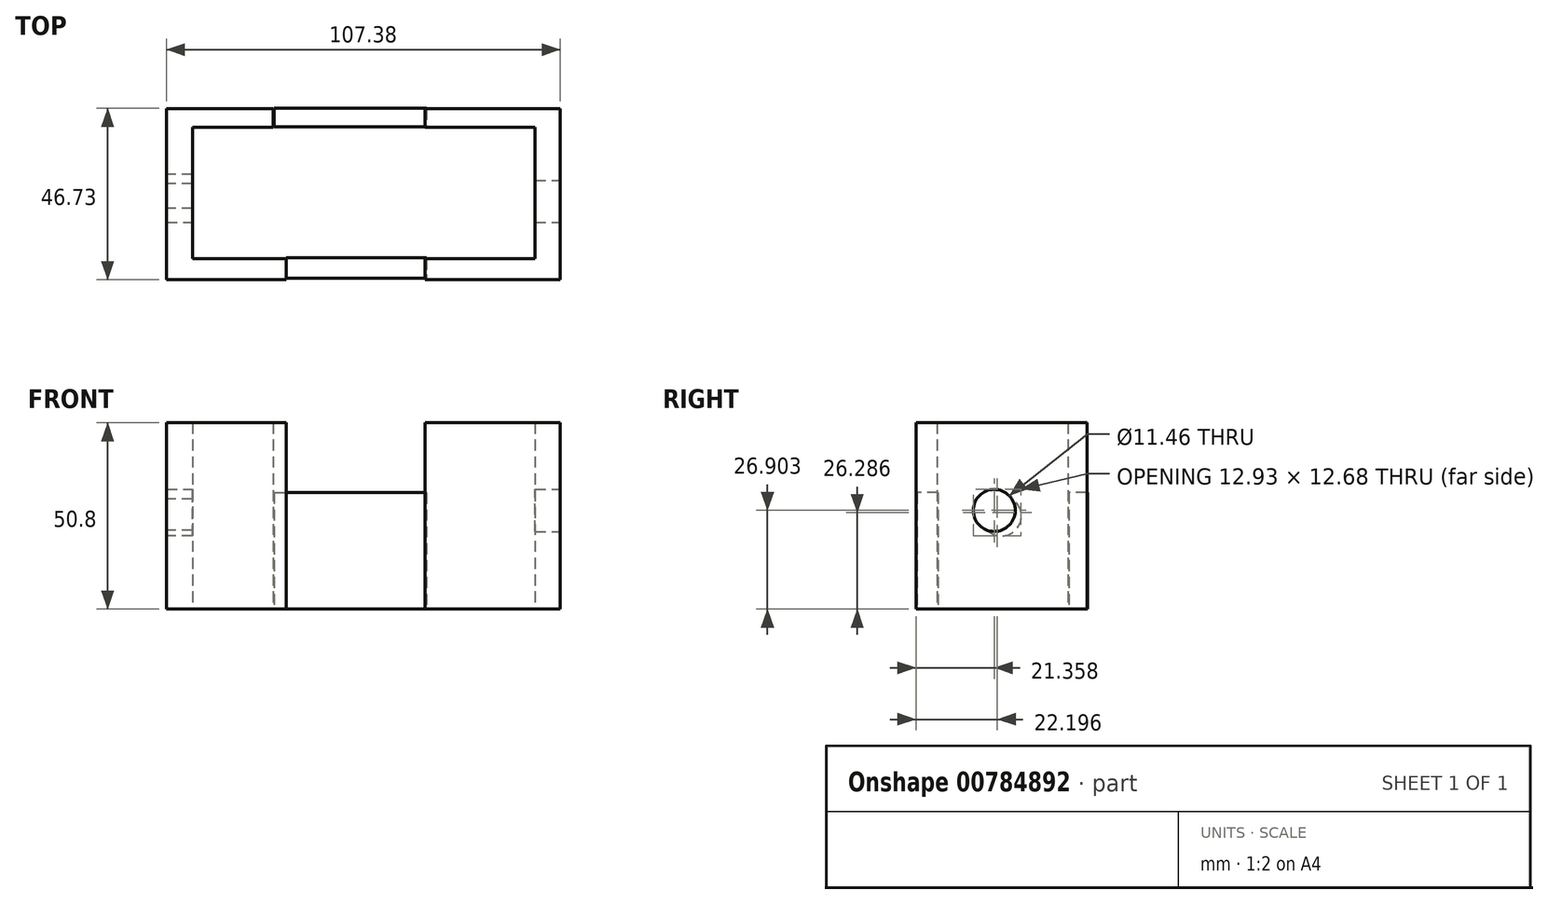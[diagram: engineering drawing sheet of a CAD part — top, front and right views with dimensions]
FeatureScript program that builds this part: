
annotation { "Feature Type Name" : "Feature", "Feature Type Description" : "" }
export const myFeature = defineFeature(function(context is Context, id is Id, definition is map)
    precondition{}
    {
        {
            var Q0;
            Q0=qCreatedBy(makeId("Top.planeOp"),FACE);
            var sketch = newSketch(context, id + "F0", { "sketchPlane" : qUnion([Q0])});
            skLineSegment(sketch, "E0.bottom", {"start": v(-52.79, 19.4) * mm, "end": v(54.6, 19.4) * mm});
            skLineSegment(sketch, "E0.top", {"start": v(-52.79, -27.22) * mm, "end": v(54.6, -27.22) * mm});
            skLineSegment(sketch, "E0.left", {"start": v(-52.79, 19.4) * mm, "end": v(-52.79, -27.22) * mm});
            skLineSegment(sketch, "E0.right", {"start": v(54.6, 19.4) * mm, "end": v(54.6, -27.22) * mm});
            skLineSegment(sketch, "E1.bottom", {"start": v(-45.57, 14.29) * mm, "end": v(47.68, 14.29) * mm});
            skLineSegment(sketch, "E1.top", {"start": v(-45.57, -21.5) * mm, "end": v(47.68, -21.5) * mm});
            skLineSegment(sketch, "E1.left", {"start": v(-45.57, 14.29) * mm, "end": v(-45.57, -21.5) * mm});
            skLineSegment(sketch, "E1.right", {"start": v(47.68, 14.29) * mm, "end": v(47.68, -21.5) * mm});
            skLineSegment(sketch, "E2", {"start": v(-20.07, -27.22) * mm, "end": v(-20.07, -21.5) * mm});
            skLineSegment(sketch, "E3", {"start": v(17.78, -27.22) * mm, "end": v(17.78, -21.5) * mm});
            skLineSegment(sketch, "E4", {"start": v(-23.62, 14.29) * mm, "end": v(-23.62, 19.4) * mm});
            skLineSegment(sketch, "E5", {"start": v(17.78, 14.29) * mm, "end": v(17.78, 19.4) * mm});
            skSolve(sketch);
        }
        {
            var Q0;
            {var subQ0=sQuery(id+"F0.wireOp",EDGE,"E0.left");Q0=makeQuery(id+"F0.imprint","IMPRINT",FACE,{"disambiguationData":[TD([[makeQuery(id+"F0.imprint","IMPRINT",EDGE,{"derivedFrom":subQ0}),1.0]])]});}
            var Q1;
            {var subQ3=sQuery(id+"F0.wireOp",EDGE,"E0.right");Q1=makeQuery(id+"F0.imprint","IMPRINT",FACE,{"disambiguationData":[TD([[makeQuery(id+"F0.imprint","IMPRINT",EDGE,{"derivedFrom":subQ3}),-1.0]])]});}
            extrude(context, id + "F1", {"entities" : qUnion([Q0, Q1]), "depth" : 50.8 * mm, "offsetDistance" : 25.4 * mm});
        }
        {
            var Q0;
            Q0=qCreatedBy(makeId("Top.planeOp"),FACE);
            var sketch = newSketch(context, id + "F2", { "sketchPlane" : qUnion([Q0])});
            skLineSegment(sketch, "E6.bottom", {"start": v(-20.08, -21.17) * mm, "end": v(18.1, -21.17) * mm});
            skLineSegment(sketch, "E6.top", {"start": v(-20.08, -26.86) * mm, "end": v(18.1, -26.86) * mm});
            skLineSegment(sketch, "E6.left", {"start": v(-20.08, -21.17) * mm, "end": v(-20.08, -26.86) * mm});
            skLineSegment(sketch, "E6.right", {"start": v(18.1, -21.17) * mm, "end": v(18.1, -26.86) * mm});
            skPoint(sketch, "E7.oppositeSnap0", {"position": v(18.1, -24.02) * mm});
            skLineSegment(sketch, "E7.bottom", {"start": v(-23.37, 19.51) * mm, "end": v(18.1, 19.51) * mm});
            skLineSegment(sketch, "E7.top", {"start": v(-23.37, 14.51) * mm, "end": v(18.1, 14.51) * mm});
            skLineSegment(sketch, "E7.left", {"start": v(-23.37, 19.51) * mm, "end": v(-23.37, 14.51) * mm});
            skLineSegment(sketch, "E7.right", {"start": v(18.1, 19.51) * mm, "end": v(18.1, 14.51) * mm});
            skSolve(sketch);
        }
        {
            var Q0;
            Q0=makeQuery(id+"F2.imprint","IMPRINT",FACE,{"disambiguationData":[TD([[makeQuery(id+"F2.imprint","IMPRINT",EDGE,{"derivedFrom":sQuery(id+"F2.wireOp",EDGE,"E7.bottom")}),-1.0]])]});
            var Q1;
            Q1=makeQuery(id+"F2.imprint","IMPRINT",FACE,{"disambiguationData":[TD([[makeQuery(id+"F2.imprint","IMPRINT",EDGE,{"derivedFrom":sQuery(id+"F2.wireOp",EDGE,"E6.bottom")}),-1.0]])]});
            extrude(context, id + "F3", {"entities" : qUnion([Q0, Q1]), "depth" : 31.75 * mm, "offsetDistance" : 25.4 * mm});
        }
        {
            var Q0;
            Q0=makeQuery(id+"F1.opExtrude","SWEPT_FACE",FACE,{"disambiguationData":[OSD([sQuery(id+"F0.wireOp",EDGE,"E0.right")])]});
            var sketch = newSketch(context, id + "F4", { "sketchPlane" : qUnion([Q0])});
            skCircle(sketch, "E8", {"center": v(-5.86, 26.9) * mm, "radius": 5.73 * mm});
            skSolve(sketch);
        }
        {
            var Q0;
            Q0=makeQuery(id+"F4.imprint","IMPRINT",FACE,{"disambiguationData":[TD([[makeQuery(id+"F4.imprint","IMPRINT",EDGE,{"derivedFrom":sQuery(id+"F4.wireOp",EDGE,"E8")}),1.0]])]});
            extrude(context, id + "F5", {"entities" : qUnion([Q0]), "operationType" : NewBodyOperationType.REMOVE, "oppositeDirection" : true, "depth" : 127 * mm, "offsetDistance" : 25.4 * mm});
        }
        {
            var Q0;
            Q0=makeQuery(id+"F1.opExtrude","SWEPT_FACE",FACE,{"disambiguationData":[OSD([sQuery(id+"F0.wireOp",EDGE,"E0.left")])]});
            var sketch = newSketch(context, id + "F6", { "sketchPlane" : qUnion([Q0])});
            skCircle(sketch, "E9", {"center": v(3.91, 25.37) * mm, "radius": 5.43 * mm});
            skPoint(sketch, "E9.centerSnap0", {"position": v(3.91, 50.8) * mm});
            skSolve(sketch);
        }
        {
            var Q0;
            Q0=makeQuery(id+"F6.imprint","IMPRINT",FACE,{"disambiguationData":[TD([[makeQuery(id+"F6.imprint","IMPRINT",EDGE,{"derivedFrom":sQuery(id+"F6.wireOp",EDGE,"E9")}),1.0]])]});
            extrude(context, id + "F7", {"entities" : qUnion([Q0]), "operationType" : NewBodyOperationType.REMOVE, "oppositeDirection" : true, "depth" : 25.4 * mm, "offsetDistance" : 25.4 * mm});
        }
    });
